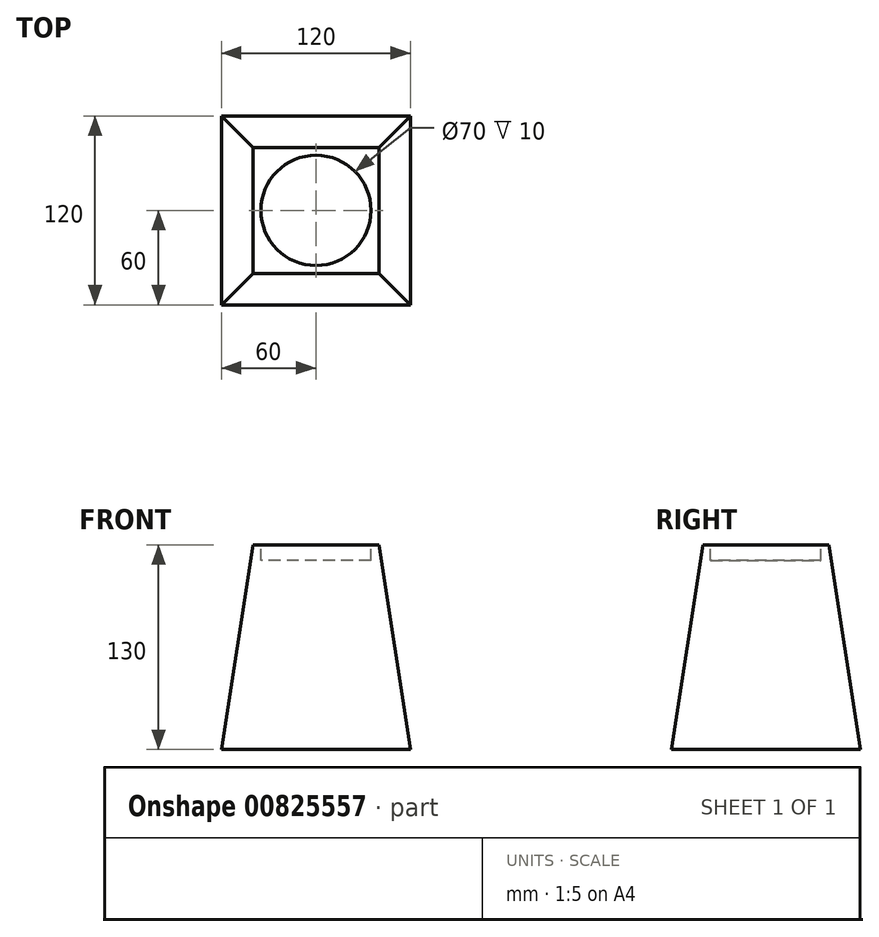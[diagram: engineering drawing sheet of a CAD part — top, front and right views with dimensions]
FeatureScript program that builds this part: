
annotation { "Feature Type Name" : "Feature", "Feature Type Description" : "" }
export const myFeature = defineFeature(function(context is Context, id is Id, definition is map)
    precondition{}
    {
        {
            var Q0;
            Q0=qCreatedBy(makeId("Top.planeOp"),FACE);
            var sketch = newSketch(context, id + "F0", { "sketchPlane" : qUnion([Q0])});
            skLineSegment(sketch, "E0.bottom", {"start": v(-60, 60) * mm, "end": v(60, 60) * mm});
            skLineSegment(sketch, "E0.top", {"start": v(-60, -60) * mm, "end": v(60, -60) * mm});
            skLineSegment(sketch, "E0.left", {"start": v(-60, 60) * mm, "end": v(-60, -60) * mm});
            skLineSegment(sketch, "E0.right", {"start": v(60, 60) * mm, "end": v(60, -60) * mm});
            skLineSegment(sketch, "E1", {"start": v(-19.76, 0) * mm, "end": v(19.57, 0) * mm, "construction": true});
            skLineSegment(sketch, "E2", {"start": v(0, 19.76) * mm, "end": v(0, -20.9) * mm, "construction": true});
            skSolve(sketch);
        }
        {
            var Q0;
            Q0=qCreatedBy(makeId("Top.planeOp"),FACE);
            cPlane(context, id + "F1", {"entities" : qUnion([Q0]), "cplaneType" : CPlaneType.OFFSET, "offset" : 130 * mm, "width" : 150 * mm, "height" : 150 * mm});
        }
        {
            var Q0;
            Q0=qCreatedBy(id+"F1.planeOp",FACE);
            var sketch = newSketch(context, id + "F2", { "sketchPlane" : qUnion([Q0])});
            skLineSegment(sketch, "E3.0", {"start": v(-19.76, 0) * mm, "end": v(19.57, 0) * mm, "construction": true});
            skLineSegment(sketch, "E3.1", {"start": v(0, 19.76) * mm, "end": v(0, -20.9) * mm, "construction": true});
            skLineSegment(sketch, "E4.bottom", {"start": v(-40, 40) * mm, "end": v(40, 40) * mm});
            skLineSegment(sketch, "E4.top", {"start": v(-40, -40) * mm, "end": v(40, -40) * mm});
            skLineSegment(sketch, "E4.left", {"start": v(-40, 40) * mm, "end": v(-40, -40) * mm});
            skLineSegment(sketch, "E4.right", {"start": v(40, 40) * mm, "end": v(40, -40) * mm});
            skSolve(sketch);
        }
        {
            var Q0;
            Q0=makeQuery(id+"F0.imprint","IMPRINT",FACE,{"disambiguationData":[TD([[makeQuery(id+"F0.imprint","IMPRINT",EDGE,{"derivedFrom":sQuery(id+"F0.wireOp",EDGE,"E0.bottom")}),-1.0]])]});
            var Q1;
            Q1=makeQuery(id+"F2.imprint","IMPRINT",FACE,{"disambiguationData":[TD([[makeQuery(id+"F2.imprint","IMPRINT",EDGE,{"derivedFrom":sQuery(id+"F2.wireOp",EDGE,"E4.bottom")}),-1.0]])]});
            loft(context, id + "F3", {"sheetProfilesArray" : [{ "sheetProfileEntities" : qUnion([Q0]) }, { "sheetProfileEntities" : qUnion([Q1]) }]});
        }
        {
            var Q0;
            Q0=makeQuery(id+"F3.opLoft","CAP_FACE",FACE,{"disambiguationData":[OSD([makeQuery(id+"F2.imprint","IMPRINT",FACE,{"disambiguationData":[TD([[makeQuery(id+"F2.imprint","IMPRINT",EDGE,{"derivedFrom":sQuery(id+"F2.wireOp",EDGE,"E4.bottom")}),-1.0]])]})])],"isStart":true});
            var sketch = newSketch(context, id + "F4", { "sketchPlane" : qUnion([Q0])});
            skPoint(sketch, "E5.0", {"position": v(0, 0) * mm});
            skCircle(sketch, "E6", {"center": v(0, 0) * mm, "radius": 35 * mm});
            skSolve(sketch);
        }
        {
            var Q0;
            Q0=makeQuery(id+"F4.imprint","IMPRINT",FACE,{"disambiguationData":[TD([[makeQuery(id+"F4.imprint","IMPRINT",EDGE,{"derivedFrom":sQuery(id+"F4.wireOp",EDGE,"E6")}),1.0]])]});
            extrude(context, id + "F5", {"entities" : qUnion([Q0]), "operationType" : NewBodyOperationType.REMOVE, "oppositeDirection" : true, "depth" : 10 * mm, "offsetDistance" : 25 * mm});
        }
    });
